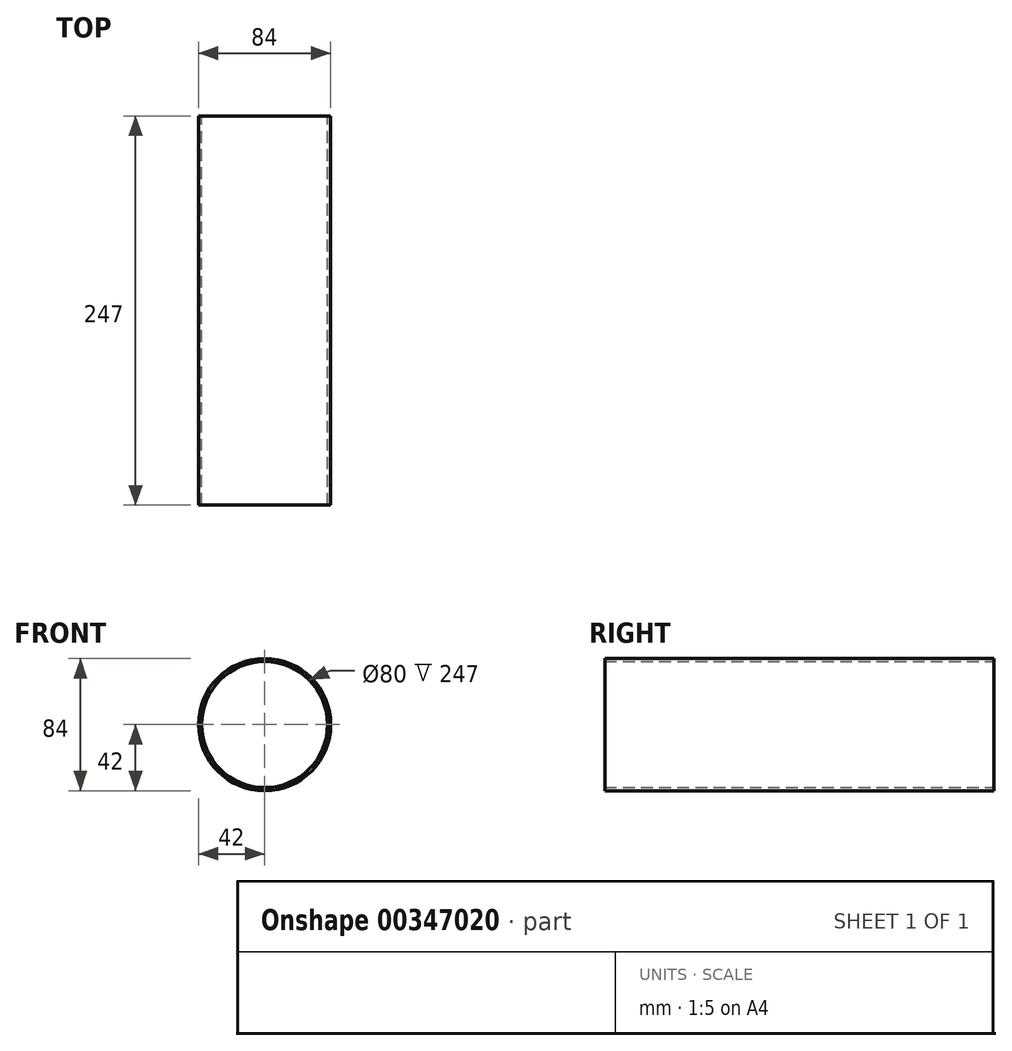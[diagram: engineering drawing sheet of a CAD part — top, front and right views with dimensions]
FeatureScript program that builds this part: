
annotation { "Feature Type Name" : "Feature", "Feature Type Description" : "" }
export const myFeature = defineFeature(function(context is Context, id is Id, definition is map)
    precondition{}
    {
        {
            var Q0;
            Q0=qCreatedBy(makeId("Front.planeOp"),FACE);
            var sketch = newSketch(context, id + "F0", { "sketchPlane" : qUnion([Q0])});
            skCircle(sketch, "E0", {"center": v(0, 0) * mm, "radius": 40 * mm});
            skCircle(sketch, "E1", {"center": v(0, 0) * mm, "radius": 42 * mm});
            skSolve(sketch);
        }
        {
            var Q0;
            Q0=makeQuery(id+"F0.imprint","IMPRINT",FACE,{"disambiguationData":[TD([[makeQuery(id+"F0.imprint","IMPRINT",EDGE,{"derivedFrom":sQuery(id+"F0.wireOp",EDGE,"E0")}),-1.0]])]});
            extrude(context, id + "F1", {"entities" : qUnion([Q0]), "endBound" : BoundingType.SYMMETRIC, "depth" : (128 + 150 - (33.5 - 18) * 2) * mm});
        }
    });
